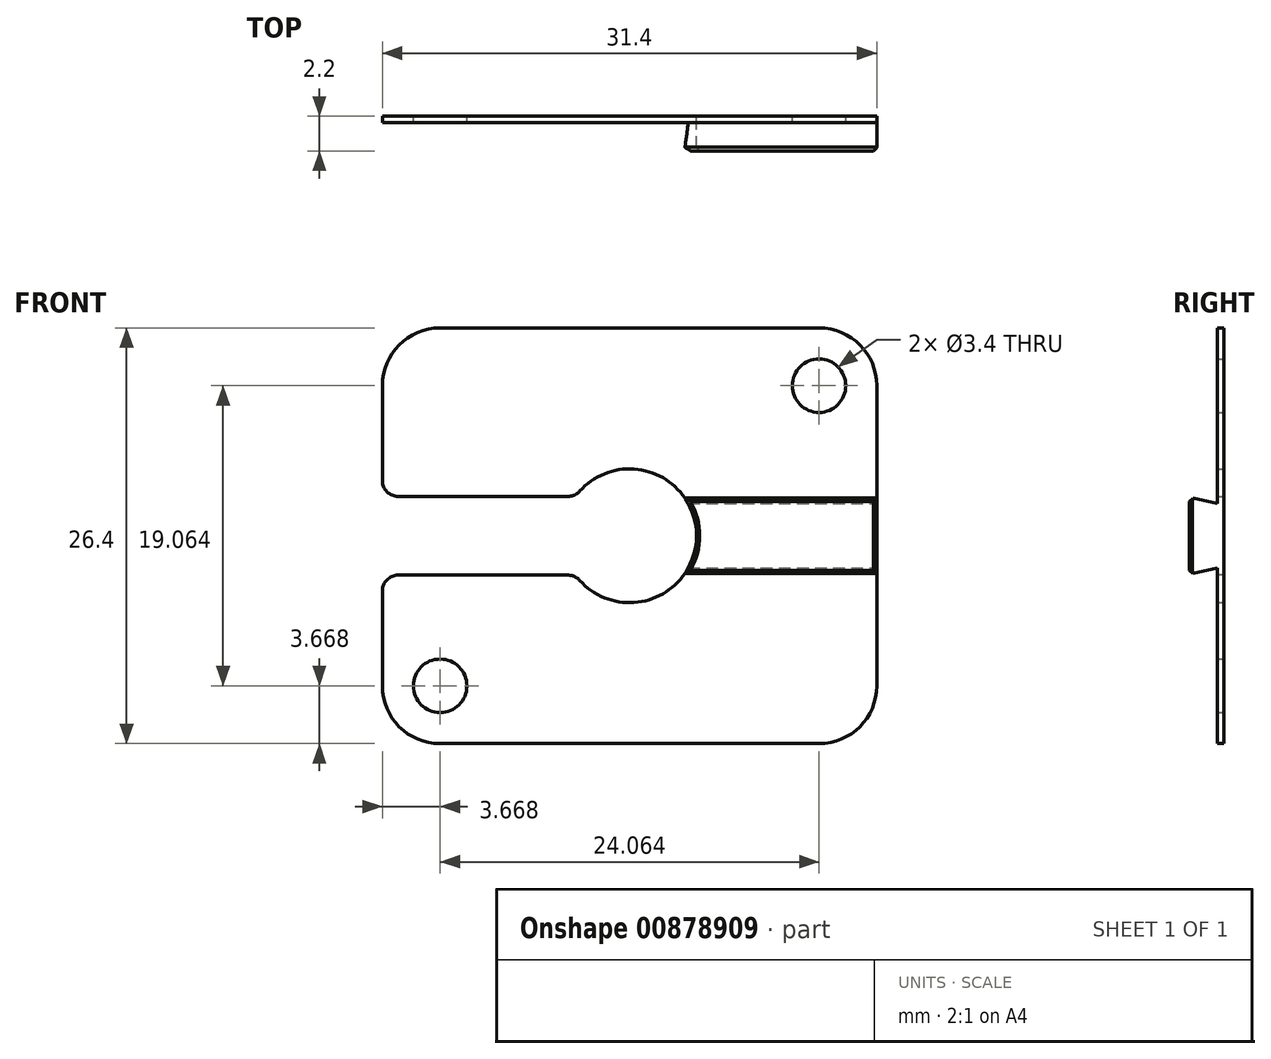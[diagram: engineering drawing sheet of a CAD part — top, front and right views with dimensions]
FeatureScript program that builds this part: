
annotation { "Feature Type Name" : "Feature", "Feature Type Description" : "" }
export const myFeature = defineFeature(function(context is Context, id is Id, definition is map)
    precondition{}
    {
        {
            var Q0;
            Q0=qCreatedBy(makeId("Front.planeOp"),FACE);
            var sketch = newSketch(context, id + "F0", { "sketchPlane" : qUnion([Q0])});
            skLineSegment(sketch, "E0.bottom", {"start": v(-15.7, 13.2) * mm, "end": v(15.7, 13.2) * mm});
            skLineSegment(sketch, "E0.top", {"start": v(-15.7, -13.2) * mm, "end": v(15.7, -13.2) * mm});
            skLineSegment(sketch, "E0.left", {"start": v(-15.7, 13.2) * mm, "end": v(-15.7, -13.2) * mm});
            skLineSegment(sketch, "E0.right", {"start": v(15.7, 13.2) * mm, "end": v(15.7, -13.2) * mm});
            skLineSegment(sketch, "E1.right", {"start": v(0, 0) * mm, "end": v(0, 13.2) * mm, "construction": true});
            skLineSegment(sketch, "E2.bottom", {"start": v(0, 0) * mm, "end": v(-15.7, 0) * mm, "construction": true});
            skLineSegment(sketch, "E2.top", {"start": v(0, 0) * mm, "end": v(-15.7, 0) * mm, "construction": true});
            skLineSegment(sketch, "E2.left", {"start": v(0, 0) * mm, "end": v(0, 0) * mm});
            skLineSegment(sketch, "E2.right", {"start": v(-15.7, 0) * mm, "end": v(-15.7, 0) * mm});
            skLineSegment(sketch, "E3", {"start": v(-12.03, 9.53) * mm, "end": v(12.03, -9.53) * mm, "construction": true});
            skCircle(sketch, "E4", {"center": v(-12.03, 9.53) * mm, "radius": 1.7 * mm, "construction": true});
            skCircle(sketch, "E5", {"center": v(12.03, -9.53) * mm, "radius": 1.7 * mm, "construction": true});
            skCircle(sketch, "E6", {"center": v(-12.03, 9.53) * mm, "radius": 3.67 * mm, "construction": true});
            skCircle(sketch, "E7", {"center": v(12.03, -9.53) * mm, "radius": 3.67 * mm, "construction": true});
            skCircle(sketch, "E8.MirrorC", {"center": v(12.03, 9.53) * mm, "radius": 1.7 * mm});
            skCircle(sketch, "E9.MirrorC", {"center": v(-12.03, -9.53) * mm, "radius": 1.7 * mm});
            skSolve(sketch);
        }
        {
            var Q0;
            Q0=qSketchRegion(id+"F0",true);
            extrude(context, id + "F1", {"entities" : qUnion([Q0]), "depth" : 0.4 * mm, "offsetDistance" : 25 * mm});
        }
        {
            var Q0;
            Q0=makeQuery(id+"F1.opExtrude","SWEPT_EDGE",EDGE,{"disambiguationData":[OSD([sQuery(id+"F0.wireOp",EDGE,"E0.top"),sQuery(id+"F0.wireOp",EDGE,"E0.right")])]});
            var Q1;
            Q1=makeQuery(id+"F1.opExtrude","SWEPT_EDGE",EDGE,{"disambiguationData":[OSD([sQuery(id+"F0.wireOp",EDGE,"E0.bottom"),sQuery(id+"F0.wireOp",EDGE,"E0.right")])]});
            var Q2;
            Q2=makeQuery(id+"F1.opExtrude","SWEPT_EDGE",EDGE,{"disambiguationData":[OSD([sQuery(id+"F0.wireOp",EDGE,"E0.top"),sQuery(id+"F0.wireOp",EDGE,"E0.left")])]});
            var Q3;
            Q3=makeQuery(id+"F1.opExtrude","SWEPT_EDGE",EDGE,{"disambiguationData":[OSD([sQuery(id+"F0.wireOp",EDGE,"E0.bottom"),sQuery(id+"F0.wireOp",EDGE,"E0.left")])]});
            fillet(context, id + "F2", {"entities" : qUnion([Q0, Q1, Q2, Q3]), "radius" : 3.66 * mm, "tangentPropagation" : true, "allowEdgeOverflow" : false});
        }
        {
            var Q0;
            Q0=qCreatedBy(makeId("Front.planeOp"),FACE);
            var sketch = newSketch(context, id + "F3", { "sketchPlane" : qUnion([Q0])});
            skArc(sketch, "E10", {"start": v(-3.44, -2.5) * mm, "mid": v(4.25, 0) * mm, "end": v(-3.44, 2.5) * mm});
            skLineSegment(sketch, "E11", {"start": v(-3.44, 2.5) * mm, "end": v(-21.94, 2.5) * mm});
            skLineSegment(sketch, "E12", {"start": v(-21.94, 2.5) * mm, "end": v(-21.94, -2.5) * mm});
            skLineSegment(sketch, "E13", {"start": v(-21.94, -2.5) * mm, "end": v(-3.44, -2.5) * mm});
            skLineSegment(sketch, "E14", {"start": v(0, 0) * mm, "end": v(-31.84, 0) * mm, "construction": true});
            skSolve(sketch);
        }
        {
            var Q0;
            Q0=qSketchRegion(id+"F3",true);
            extrude(context, id + "F4", {"entities" : qUnion([Q0]), "operationType" : NewBodyOperationType.REMOVE, "depth" : 25 * mm, "offsetDistance" : 25 * mm});
        }
        {
            var Q0;
            Q0=makeQuery(id+"F4.boolean.opBoolean","COPY",EDGE,{"derivedFrom":makeQuery(id+"F4.opExtrude","SWEPT_EDGE",EDGE,{"disambiguationData":[OSD([sQuery(id+"F3.wireOp",EDGE,"E10"),sQuery(id+"F3.wireOp",EDGE,"E13")])]})});
            var Q1;
            Q1=makeQuery(id+"F4.boolean.opBoolean","COPY",EDGE,{"derivedFrom":makeQuery(id+"F4.opExtrude","SWEPT_EDGE",EDGE,{"disambiguationData":[OSD([sQuery(id+"F3.wireOp",EDGE,"E10"),sQuery(id+"F3.wireOp",EDGE,"E11")])]})});
            var Q2;
            Q2=makeQuery(id+"F4.boolean.opBoolean","INTERSECT",EDGE,{"derivedFrom":[makeQuery(id+"F1.opExtrude","SWEPT_FACE",FACE,{"disambiguationData":[OSD([sQuery(id+"F0.wireOp",EDGE,"E0.left")])]}),makeQuery(id+"F4.opExtrude","SWEPT_FACE",FACE,{"disambiguationData":[OSD([sQuery(id+"F3.wireOp",EDGE,"E11")])]})]});
            var Q3;
            Q3=makeQuery(id+"F4.boolean.opBoolean","INTERSECT",EDGE,{"derivedFrom":[makeQuery(id+"F1.opExtrude","SWEPT_FACE",FACE,{"disambiguationData":[OSD([sQuery(id+"F0.wireOp",EDGE,"E0.left")])]}),makeQuery(id+"F4.opExtrude","SWEPT_FACE",FACE,{"disambiguationData":[OSD([sQuery(id+"F3.wireOp",EDGE,"E13")])]})]});
            fillet(context, id + "F5", {"entities" : qUnion([Q0, Q1, Q2, Q3]), "radius" : 1 * mm, "tangentPropagation" : true, "allowEdgeOverflow" : false});
        }
        {
            var Q0;
            Q0=makeQuery(id+"F1.opExtrude","CAP_FACE",FACE,{"disambiguationData":[OSD([sQuery(id+"F0.wireOp",EDGE,"E0.bottom"),sQuery(id+"F0.wireOp",EDGE,"E0.top"),sQuery(id+"F0.wireOp",EDGE,"E0.left"),sQuery(id+"F0.wireOp",EDGE,"E0.right"),sQuery(id+"F0.wireOp",EDGE,"E4"),sQuery(id+"F0.wireOp",EDGE,"E5")])],"isStart":true});
            var sketch = newSketch(context, id + "F6", { "sketchPlane" : qUnion([Q0])});
            skLineSegment(sketch, "E15", {"start": v(-15.7, 2.44) * mm, "end": v(-3.48, 2.44) * mm});
            skLineSegment(sketch, "E16", {"start": v(-15.7, -2.44) * mm, "end": v(-3.48, -2.44) * mm});
            skLineSegment(sketch, "E17", {"start": v(-17.91, 0) * mm, "end": v(0, 0) * mm, "construction": true});
            skPoint(sketch, "E17.startSnap0", {"position": v(-15.7, 0) * mm});
            skArc(sketch, "E18.0", {"start": v(-3.48, -2.44) * mm, "mid": v(-4.25, 0) * mm, "end": v(-3.48, 2.44) * mm});
            skLineSegment(sketch, "E19", {"start": v(-15.7, 2.44) * mm, "end": v(-15.7, -2.44) * mm});
            skPoint(sketch, "E20.orphan", {"position": v(3.17, 2.83) * mm});
            skPoint(sketch, "E21.orphan", {"position": v(3.17, -2.83) * mm});
            skSolve(sketch);
        }
        {
            var Q0;
            Q0=qSketchRegion(id+"F6",true);
            extrude(context, id + "F7", {"entities" : qUnion([Q0]), "operationType" : NewBodyOperationType.ADD, "oppositeDirection" : true, "depth" : 2.2 * mm, "offsetDistance" : 25 * mm});
        }
        {
            var Q0;
            Q0=makeQuery(id+"F7.boolean.opBoolean","MERGE",FACE,{"derivedFrom":[makeQuery(id+"F1.opExtrude","SWEPT_FACE",FACE,{"disambiguationData":[OSD([sQuery(id+"F0.wireOp",EDGE,"E0.right")])]}),makeQuery(id+"F7.opExtrude","SWEPT_FACE",FACE,{"disambiguationData":[OSD([sQuery(id+"F6.wireOp",EDGE,"E19")])]})]});
            var sketch = newSketch(context, id + "F8", { "sketchPlane" : qUnion([Q0])});
            skLineSegment(sketch, "E22", {"start": v(-2.2, 2.44) * mm, "end": v(-0.4, 2.04) * mm});
            skLineSegment(sketch, "E23", {"start": v(-0.4, 2.04) * mm, "end": v(-0.4, 2.44) * mm});
            skLineSegment(sketch, "E24", {"start": v(-0.4, 2.44) * mm, "end": v(-2.2, 2.44) * mm});
            skLineSegment(sketch, "E25", {"start": v(-2.2, -2.44) * mm, "end": v(-0.4, -2.44) * mm});
            skLineSegment(sketch, "E26", {"start": v(-0.4, -2.44) * mm, "end": v(-0.4, -2.04) * mm});
            skLineSegment(sketch, "E27", {"start": v(-0.4, -2.04) * mm, "end": v(-2.2, -2.44) * mm});
            skLineSegment(sketch, "E28", {"start": v(0, 0) * mm, "end": v(-5.51, 0) * mm, "construction": true});
            skSolve(sketch);
        }
        {
            var Q0;
            Q0=qSketchRegion(id+"F8",true);
            extrude(context, id + "F9", {"entities" : qUnion([Q0]), "operationType" : NewBodyOperationType.REMOVE, "oppositeDirection" : true, "depth" : 25 * mm, "offsetDistance" : 25 * mm});
        }
        {
            var Q0;
            Q0=makeQuery(id+"F7.opExtrude","CAP_FACE",FACE,{"disambiguationData":[OSD([sQuery(id+"F6.wireOp",EDGE,"E15"),sQuery(id+"F6.wireOp",EDGE,"E16"),sQuery(id+"F6.wireOp",EDGE,"E18.0"),sQuery(id+"F6.wireOp",EDGE,"E19")])],"isStart":false});
            chamfer(context, id + "F10", {"entities" : qUnion([Q0]), "width" : .2 * mm, "tangentPropagation" : true});
        }
    });
